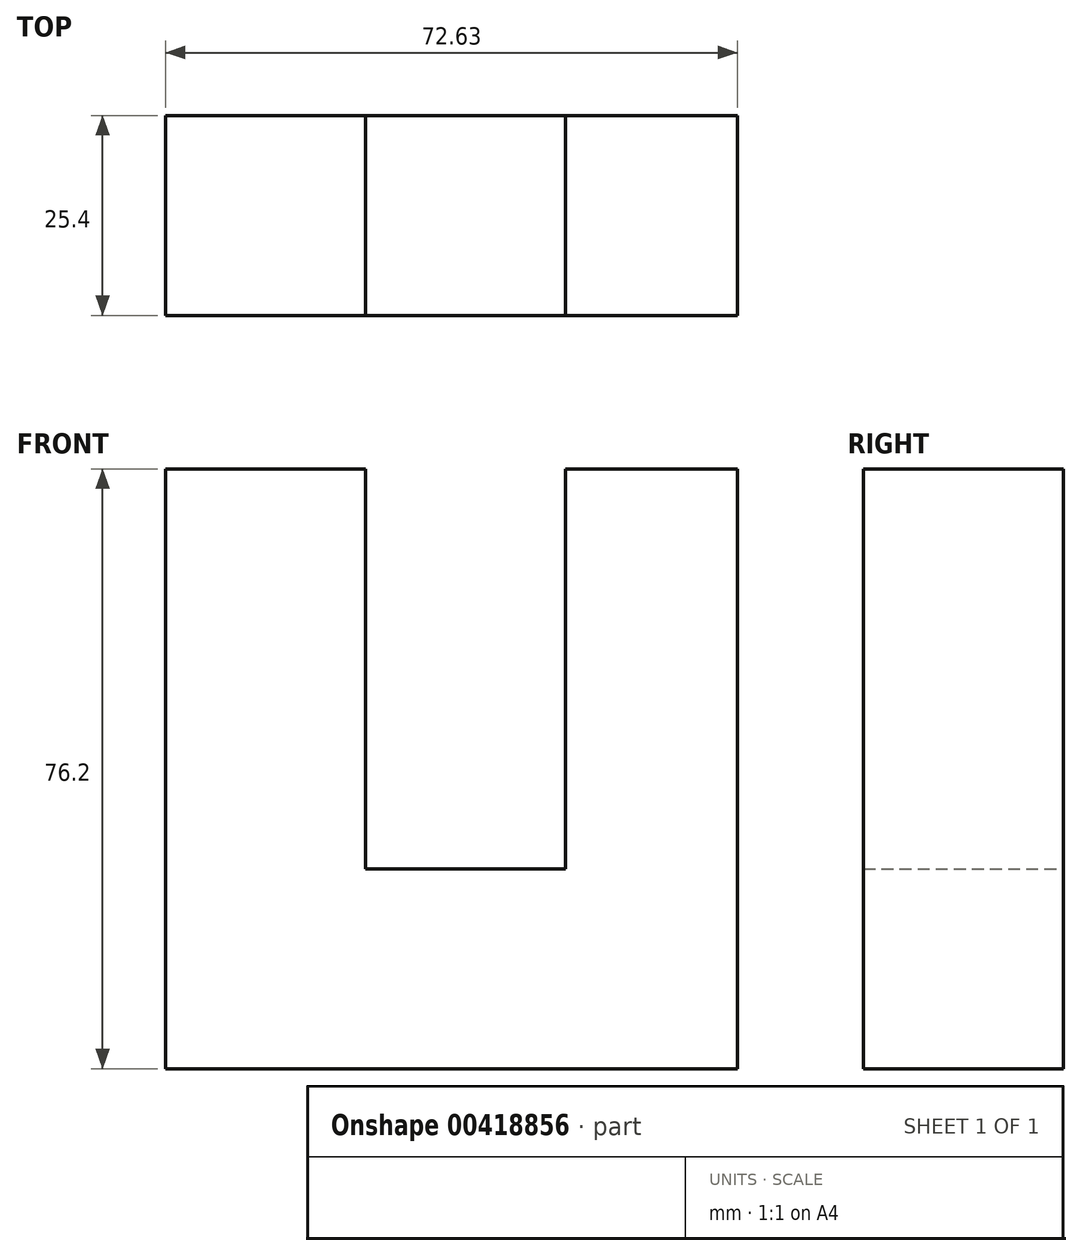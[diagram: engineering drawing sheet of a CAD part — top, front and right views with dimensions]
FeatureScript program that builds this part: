
annotation { "Feature Type Name" : "Feature", "Feature Type Description" : "" }
export const myFeature = defineFeature(function(context is Context, id is Id, definition is map)
    precondition{}
    {
        {
            var Q0;
            Q0=qCreatedBy(makeId("Front.planeOp"),FACE);
            var sketch = newSketch(context, id + "F0", { "sketchPlane" : qUnion([Q0])});
            skLineSegment(sketch, "E0", {"start": v(3.57, 0) * mm, "end": v(-72.63, 0) * mm});
            skLineSegment(sketch, "E1", {"start": v(-72.63, 0) * mm, "end": v(-72.63, 76.2) * mm});
            skLineSegment(sketch, "E2", {"start": v(-72.63, 76.2) * mm, "end": v(-47.23, 76.2) * mm});
            skLineSegment(sketch, "E3", {"start": v(-47.23, 76.2) * mm, "end": v(-47.23, 25.4) * mm});
            skLineSegment(sketch, "E4", {"start": v(-47.23, 25.4) * mm, "end": v(-21.83, 25.4) * mm});
            skLineSegment(sketch, "E5", {"start": v(-21.83, 25.4) * mm, "end": v(-21.83, 76.2) * mm});
            skLineSegment(sketch, "E6", {"start": v(-21.83, 76.2) * mm, "end": v(0, 76.2) * mm});
            skLineSegment(sketch, "E7", {"start": v(0, 76.2) * mm, "end": v(0, 0) * mm});
            skSolve(sketch);
        }
        {
            var Q0;
            Q0 = qSketchRegion(id + "F0", true);
            var Q1;
            {var subQ0=sQuery(id+"F0.wireOp",EDGE,"E1");Q1=makeQuery(id+"F0.imprint","IMPRINT",FACE,{"disambiguationData":[TD([[makeQuery(id+"F0.imprint","IMPRINT",EDGE,{"derivedFrom":subQ0}),-1.0]])]});}
            extrude(context, id + "F1", {"entities" : qUnion([Q0, Q1]), "depth" : 25.4 * mm});
        }
    });
